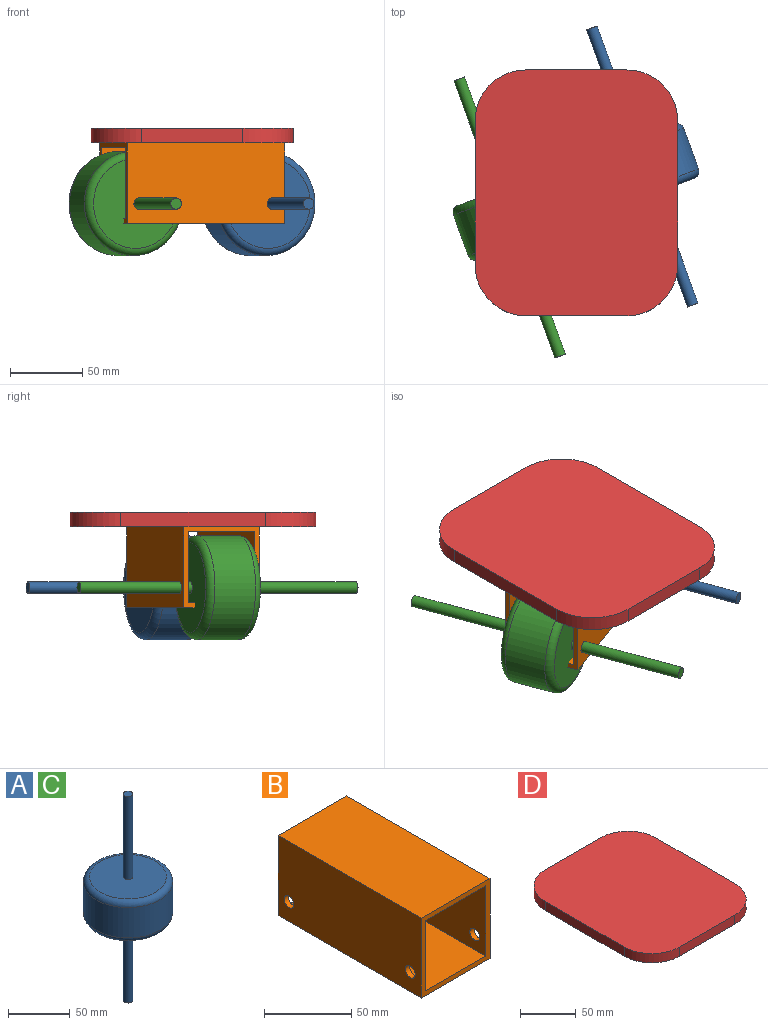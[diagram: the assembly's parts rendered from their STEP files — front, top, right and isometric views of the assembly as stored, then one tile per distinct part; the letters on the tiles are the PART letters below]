
ASSEMBLY  parts=4 mates=4
PART A: 9 faces, bbox 77.9x77.9x204 mm
  f0: cylinder r=36mm len=72mm, axis (0,0,-1), area 6785.8mm2, adj f3,f4
  f1: plane 62x62mm, normal (0,0,1), area 2971.3mm2, adj f4,f7
  f2: plane 62x62mm, normal (0,0,-1), area 2971.3mm2, adj f3,f6
  f3: torus R=31mm, axis (0,0,1), area 1686.9mm2, adj f0,f2
  f4: torus R=31mm, axis (0,0,1), area 1686.9mm2, adj f0,f1
  f5: plane 7.8x7.8mm, normal (0,0,-1), area 47.8mm2, adj f6
  f6: cylinder r=3.9mm len=82mm, axis (0,0,-1), area 2009.4mm2, adj f2,f5
  f7: cylinder r=3.9mm len=82mm, axis (0,0,-1), area 2009.4mm2, adj f1,f8
  f8: plane 7.8x7.8mm, normal (0,0,1), area 47.8mm2, adj f7
PART B: 14 faces, bbox 55.6x116x56 mm
  f0: plane 56x55.6mm, normal (0,-1,0), area 712.6mm2, adj f2,f3,f4,f5,f6,f7,f8,f9
  f1: plane 56x55.6mm, normal (0,1,0), area 712.6mm2, adj f2,f3,f4,f5,f6,f7,f8,f9
  f2: plane 116x55.6mm, normal (0,0,1), area 6449.6mm2, adj f0,f1,f3,f5
  f3: plane 116x56mm, normal (-1,0,0), area 6395.5mm2, adj f0,f1,f2,f4,f12,f13
  f4: plane 116x55.6mm, normal (0,0,-1), area 6449.6mm2, adj f0,f1,f3,f5
  f5: plane 116x56mm, normal (1,0,0), area 6395.5mm2, adj f0,f1,f2,f4,f10,f11
  f6: plane 116x48.8mm, normal (0,0,-1), area 5660.8mm2, adj f0,f1,f7,f9
  f7: plane 116x49.2mm, normal (1,0,0), area 5606.7mm2, adj f0,f1,f6,f8,f12,f13
  f8: plane 116x48.8mm, normal (0,0,1), area 5660.8mm2, adj f0,f1,f7,f9
  f9: plane 116x49.2mm, normal (-1,0,0), area 5606.7mm2, adj f0,f1,f6,f8,f10,f11
  f10: cylinder r=4mm len=8mm, axis (1,0,0), area 85.5mm2, adj f5,f9
  f11: cylinder r=4mm len=8mm, axis (1,0,0), area 85.5mm2, adj f5,f9
  f12: cylinder r=4mm len=8mm, axis (1,0,0), area 85.5mm2, adj f3,f7
  f13: cylinder r=4mm len=8mm, axis (1,0,0), area 85.5mm2, adj f3,f7
PART C: same geometry as A
PART D: 10 faces, bbox 140x170x10 mm
  f0: plane 70x10mm, normal (0,1,0), area 700mm2, adj f4,f5,f6,f9
  f1: plane 100x10mm, normal (-1,0,0), area 1000mm2, adj f4,f5,f6,f7
  f2: plane 70x10mm, normal (0,-1,0), area 700mm2, adj f4,f5,f7,f8
  f3: plane 100x10mm, normal (1,0,0), area 1000mm2, adj f4,f5,f8,f9
  f4: plane 170x140mm, normal (0,0,1), area 22748.5mm2, adj f0,f1,f2,f3,f6,f7,f8,f9
  f5: plane 170x140mm, normal (0,0,-1), area 22748.5mm2, adj f0,f1,f2,f3,f6,f7,f8,f9
  f6: cylinder r=35mm len=35mm, axis (0,0,1), area 549.8mm2, adj f0,f1,f4,f5
  f7: cylinder r=35mm len=35mm, axis (0,0,-1), area 549.8mm2, adj f1,f2,f4,f5
  f8: cylinder r=35mm len=35mm, axis (0,0,1), area 549.8mm2, adj f2,f3,f4,f5
  f9: cylinder r=35mm len=35mm, axis (0,0,-1), area 549.8mm2, adj f0,f3,f4,f5
PLACE A rot(axis=(0.63,-0.44,0.63),132.1deg) t=(15.25,-0.99,10.85)mm
PLACE B rot(axis=(0,0,1),110deg) t=(-30.33,-19.33,52.85)mm
PLACE C rot(axis=(0.63,-0.44,0.63),132.1deg) t=(-76.41,-36.27,10.85)mm
PLACE D t=(-30.33,-19.33,52.85)mm fixed
MATE revolute B.f2 <-> D.f5  axis (0,0,1) through (-30.33,-19.33,52.85)mm
MATE planar D.f5 <-> B.f2  axis (0,0,-1) through (-30.33,-104.33,52.85)mm
MATE slider A.f6 <-> B.f11  axis (-0.34,0.94,0) through (22.09,-19.79,10.85)mm
MATE slider C.f6 <-> B.f10  axis (-0.34,0.94,0) through (-41.53,-132.12,10.85)mm
